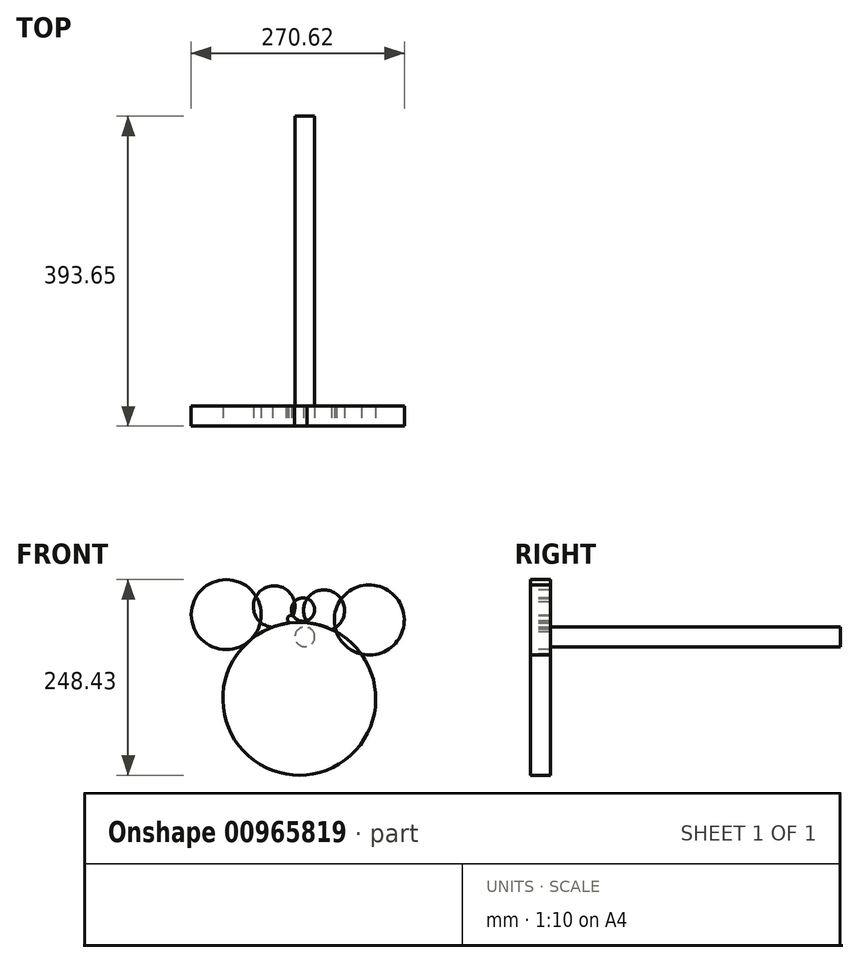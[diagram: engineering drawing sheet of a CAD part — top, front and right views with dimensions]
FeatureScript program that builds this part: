
annotation { "Feature Type Name" : "Feature", "Feature Type Description" : "" }
export const myFeature = defineFeature(function(context is Context, id is Id, definition is map)
    precondition{}
    {
        {
            var Q0;
            Q0=qCreatedBy(makeId("Front.planeOp"),FACE);
            var sketch = newSketch(context, id + "F0", { "sketchPlane" : qUnion([Q0])});
            skCircle(sketch, "E0", {"center": v(0, -5.67) * mm, "radius": 97.1 * mm});
            skCircle(sketch, "E1", {"center": v(88.92, 94.43) * mm, "radius": 44.45 * mm});
            skCircle(sketch, "E2", {"center": v(-92.8, 101.2) * mm, "radius": 44.45 * mm});
            skSolve(sketch);
        }
        {
            var Q0;
            {var subQ0=sQuery(id+"F0.wireOp",EDGE,"E0");var subQ1=makeQuery(id+"F0.imprint","INTERSECT",VERTEX,{"derivedFrom":[subQ0,sQuery(id+"F0.wireOp",EDGE,"E2")]});Q0=makeQuery(id+"F0.imprint","IMPRINT",FACE,{"disambiguationData":[TD([[makeQuery(id+"F0.imprint","IMPRINT",EDGE,{"disambiguationData":[TD([[subQ1,1.0]])],"derivedFrom":subQ0}),1.0]])]});}
            var sketch = newSketch(context, id + "F1", { "sketchPlane" : qUnion([Q0])});
            skCircle(sketch, "E3", {"center": v(4.77, 107.58) * mm, "radius": 14.8 * mm});
            skCircle(sketch, "E4", {"center": v(-31.96, 111.47) * mm, "radius": 26.41 * mm});
            skCircle(sketch, "E5", {"center": v(31.43, 106.6) * mm, "radius": 26.07 * mm});
            skCircle(sketch, "E6", {"center": v(-6.01, 70.61) * mm, "radius": 9.96 * mm});
            skCircle(sketch, "E7", {"center": v(-10.6, 95.93) * mm, "radius": 4.5 * mm});
            skSolve(sketch);
        }
        {
            var Q0;
            {var subQ0=sQuery(id+"F1.wireOp",EDGE,"E3");var subQ4=sQuery(id+"F1.wireOp",EDGE,"E4");var subQ6=makeQuery(id+"F1.imprint","INTERSECT",VERTEX,{"disambiguationData":[OD(0.0)],"derivedFrom":[subQ0,subQ4]});Q0=makeQuery(id+"F1.imprint","IMPRINT",FACE,{"disambiguationData":[TD([[makeQuery(id+"F1.imprint","IMPRINT",EDGE,{"disambiguationData":[TD([[subQ6,1.0]])],"derivedFrom":subQ0}),1.0]])]});}
            var Q1;
            {var subQ0=sQuery(id+"F1.wireOp",EDGE,"E4");var subQ1=sQuery(id+"F1.wireOp",EDGE,"E3");var subQ9=makeQuery(id+"F1.imprint","INTERSECT",VERTEX,{"disambiguationData":[OD(0.0)],"derivedFrom":[subQ1,subQ0]});Q1=makeQuery(id+"F1.imprint","IMPRINT",FACE,{"disambiguationData":[TD([[makeQuery(id+"F1.imprint","IMPRINT",EDGE,{"disambiguationData":[TD([[subQ9,-1.0]])],"derivedFrom":subQ1}),-1.0]])]});}
            var Q2;
            Q2=makeQuery(id+"F0.imprint","IMPRINT",FACE,{"disambiguationData":[TD([[makeQuery(id+"F0.imprint","IMPRINT",EDGE,{"derivedFrom":sQuery(id+"F0.wireOp",EDGE,"E2")}),1.0]])]});
            var Q3;
            {var subQ0=sQuery(id+"F0.wireOp",EDGE,"E0");var subQ1=makeQuery(id+"F0.imprint","INTERSECT",VERTEX,{"derivedFrom":[subQ0,sQuery(id+"F0.wireOp",EDGE,"E2")]});Q3=makeQuery(id+"F0.imprint","IMPRINT",FACE,{"disambiguationData":[TD([[makeQuery(id+"F0.imprint","IMPRINT",EDGE,{"disambiguationData":[TD([[subQ1,1.0]])],"derivedFrom":subQ0}),1.0]])]});}
            var Q4;
            {var subQ0=sQuery(id+"F0.wireOp",EDGE,"E1");var subQ1=sQuery(id+"F0.wireOp",EDGE,"E0");var subQ2=makeQuery(id+"F0.imprint","INTERSECT",VERTEX,{"disambiguationData":[OD(0.0)],"derivedFrom":[subQ1,subQ0]});Q4=makeQuery(id+"F0.imprint","IMPRINT",FACE,{"disambiguationData":[TD([[makeQuery(id+"F0.imprint","IMPRINT",EDGE,{"disambiguationData":[TD([[subQ2,1.0]])],"derivedFrom":subQ1}),-1.0]])]});}
            var Q5;
            {var subQ0=sQuery(id+"F1.wireOp",EDGE,"E5");var subQ1=sQuery(id+"F1.wireOp",EDGE,"E3");var subQ2=makeQuery(id+"F1.imprint","INTERSECT",VERTEX,{"disambiguationData":[OD(0.0)],"derivedFrom":[subQ1,subQ0]});Q5=makeQuery(id+"F1.imprint","IMPRINT",FACE,{"disambiguationData":[TD([[makeQuery(id+"F1.imprint","IMPRINT",EDGE,{"disambiguationData":[TD([[subQ2,1.0]])],"derivedFrom":subQ1}),-1.0]])]});}
            extrude(context, id + "F2", {"entities" : qUnion([Q0, Q1, Q2, Q3, Q4, Q5]), "oppositeDirection" : true, "depth" : 25.4 * mm, "offsetDistance" : 25.4 * mm});
        }
        {
            var Q0;
            {var subQ0=sQuery(id+"F0.wireOp",EDGE,"E1");var subQ1=sQuery(id+"F0.wireOp",EDGE,"E0");var subQ2=makeQuery(id+"F0.imprint","INTERSECT",VERTEX,{"disambiguationData":[OD(0.0)],"derivedFrom":[subQ1,subQ0]});var subQ4=makeQuery(id+"F0.imprint","INTERSECT",VERTEX,{"derivedFrom":[subQ1,sQuery(id+"F0.wireOp",EDGE,"E2")]});Q0=makeQuery(id+"F2.opExtrude","CAP_FACE",FACE,{"disambiguationData":[OSD([subQ1,subQ0]),TDD([makeQuery(id+"F0.imprint","IMPRINT",EDGE,{"disambiguationData":[TD([[subQ4,1.0]])],"derivedFrom":subQ1}),makeQuery(id+"F0.imprint","IMPRINT",EDGE,{"disambiguationData":[TD([[subQ4,-1.0]])],"derivedFrom":subQ1}),makeQuery(id+"F0.imprint","IMPRINT",EDGE,{"disambiguationData":[TD([[subQ2,-1.0]])],"derivedFrom":subQ0})])],"isStart":false});}
            var sketch = newSketch(context, id + "F3", { "sketchPlane" : qUnion([Q0])});
            skCircle(sketch, "E8", {"center": v(-7.06, 73.05) * mm, "radius": 12.53 * mm});
            skSolve(sketch);
        }
        {
            var Q0;
            Q0=makeQuery(id+"F3.imprint","IMPRINT",FACE,{"disambiguationData":[TD([[makeQuery(id+"F3.imprint","IMPRINT",EDGE,{"derivedFrom":sQuery(id+"F3.wireOp",EDGE,"E8")}),1.0]])]});
            extrude(context, id + "F4", {"entities" : qUnion([Q0]), "operationType" : NewBodyOperationType.ADD, "endBound" : BoundingType.THROUGH_ALL, "depth" : 25.4 * mm, "offsetDistance" : 25.4 * mm});
        }
    });
